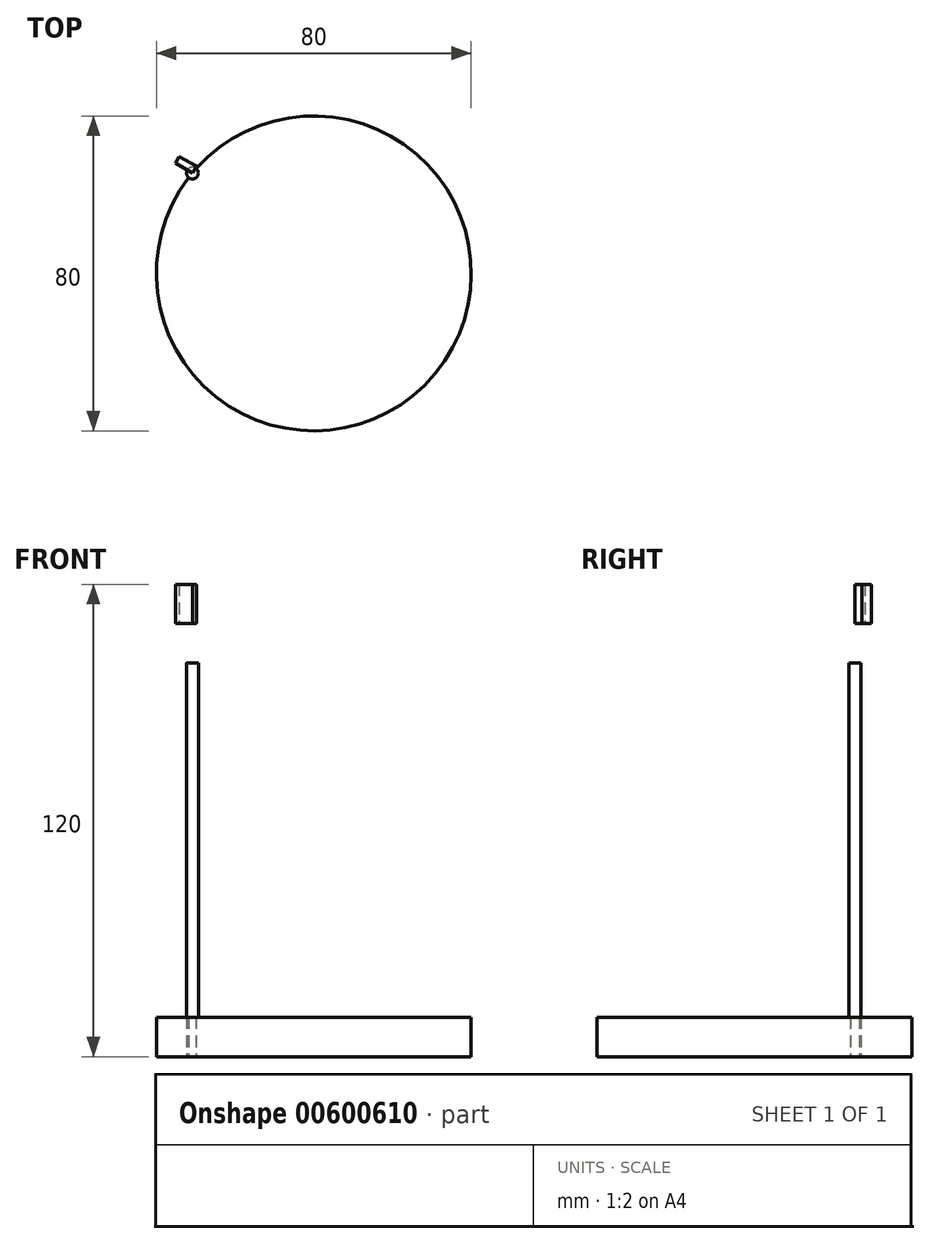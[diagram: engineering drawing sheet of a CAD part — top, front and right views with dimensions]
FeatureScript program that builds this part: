
annotation { "Feature Type Name" : "Feature", "Feature Type Description" : "" }
export const myFeature = defineFeature(function(context is Context, id is Id, definition is map)
    precondition{}
    {
        {
            var Q0;
            Q0=qCreatedBy(makeId("Top.planeOp"),FACE);
            var sketch = newSketch(context, id + "F0", { "sketchPlane" : qUnion([Q0])});
            skCircle(sketch, "E0", {"center": v(0, 0) * mm, "radius": 20 * mm});
            skCircle(sketch, "E1", {"center": v(-15.42, 12.74) * mm, "radius": 0.75 * mm});
            skSolve(sketch);
        }
        {
            var Q0;
            Q0=makeQuery(id+"F0.imprint","IMPRINT",FACE,{"disambiguationData":[TD([[makeQuery(id+"F0.imprint","IMPRINT",EDGE,{"derivedFrom":sQuery(id+"F0.wireOp",EDGE,"E0")}),1.0]])]});
            var Q1;
            Q1=makeQuery(id+"F0.imprint","IMPRINT",FACE,{"disambiguationData":[TD([[makeQuery(id+"F0.imprint","IMPRINT",EDGE,{"derivedFrom":sQuery(id+"F0.wireOp",EDGE,"E1")}),1.0]])]});
            extrude(context, id + "F1", {"entities" : qUnion([Q0, Q1]), "depth" : 5 * mm, "offsetDistance" : 25 * mm});
        }
        {
            var Q0;
            Q0=makeQuery(id+"F0.imprint","IMPRINT",FACE,{"disambiguationData":[TD([[makeQuery(id+"F0.imprint","IMPRINT",EDGE,{"derivedFrom":sQuery(id+"F0.wireOp",EDGE,"E1")}),1.0]])]});
            extrude(context, id + "F2", {"entities" : qUnion([Q0]), "operationType" : NewBodyOperationType.ADD, "depth" : 50 * mm, "offsetDistance" : 25 * mm});
        }
        {
            var Q0;
            Q0=makeQuery(id+"F2.opExtrude","CAP_FACE",FACE,{"disambiguationData":[OSD([sQuery(id+"F0.wireOp",EDGE,"E1")])],"isStart":false});
            var sketch = newSketch(context, id + "F3", { "sketchPlane" : qUnion([Q0])});
            skLineSegment(sketch, "E2.bottom", {"start": v(-12.92, 11.74) * mm, "end": v(-17.92, 11.74) * mm});
            skLineSegment(sketch, "E2.top", {"start": v(-12.92, 13.74) * mm, "end": v(-17.92, 13.74) * mm});
            skLineSegment(sketch, "E2.left", {"start": v(-12.92, 11.74) * mm, "end": v(-12.92, 13.74) * mm});
            skLineSegment(sketch, "E2.right", {"start": v(-17.92, 11.74) * mm, "end": v(-17.92, 13.74) * mm});
            skPoint(sketch, "E2.middle", {"position": v(-15.42, 12.74) * mm});
            skSolve(sketch);
        }
        {
            var Q0;
            Q0 = qSketchRegion(id + "F3", true);
            extrude(context, id + "F4", {"entities" : qUnion([Q0]), "depth" : 10 * mm, "offsetDistance" : 25 * mm});
        }
        {
            var Q0;
            Q0=makeQuery(id+"F4.opExtrude","SWEPT_BODY",BODY,{"disambiguationData":[OSD([sQuery(id+"F3.wireOp",EDGE,"E2.bottom"),sQuery(id+"F3.wireOp",EDGE,"E2.top"),sQuery(id+"F3.wireOp",EDGE,"E2.left"),sQuery(id+"F3.wireOp",EDGE,"E2.right")])]});
            var Q1;
            {var subQ0=sQuery(id+"F0.wireOp",EDGE,"E1");Q1=makeQuery(id+"F2.boolean.opBoolean","MERGE",FACE,{"derivedFrom":[makeQuery(id+"F1.opExtrude","SWEPT_FACE",FACE,{"disambiguationData":[OSD([subQ0])]}),makeQuery(id+"F2.opExtrude","SWEPT_FACE",FACE,{"disambiguationData":[OSD([subQ0])]})]});}
            transform(context, id + "F5", {"entities" : qUnion([Q0]), "transformType" : TransformType.ROTATION, "transformAxis" : qUnion([Q1]), "angle" : 30 * degree, "makeCopy" : false});
        }
        {
            var Q0;
            Q0=makeQuery(id+"F1.opExtrude","SWEPT_BODY",BODY,{"disambiguationData":[OSD([sQuery(id+"F0.wireOp",EDGE,"E0"),sQuery(id+"F0.wireOp",EDGE,"E1")])]});
            var Q1;
            Q1=sQuery(id+"F0.wireOp",VERTEX,"E0.center");
            var Q2;
            Q2=makeQuery(id+"F4.opExtrude","CAP_VERTEX",VERTEX,{"disambiguationData":[OSD([sQuery(id+"F3.wireOp",EDGE,"E2.top"),sQuery(id+"F3.wireOp",EDGE,"E2.right")])],"isStart":false});
            transform(context, id + "F6", {"entities" : qUnion([Q0]), "transformType" : TransformType.SCALE_UNIFORMLY, "scale" : 2, "scalePoint" : qUnion([Q2]), "makeCopy" : false});
        }
    });
